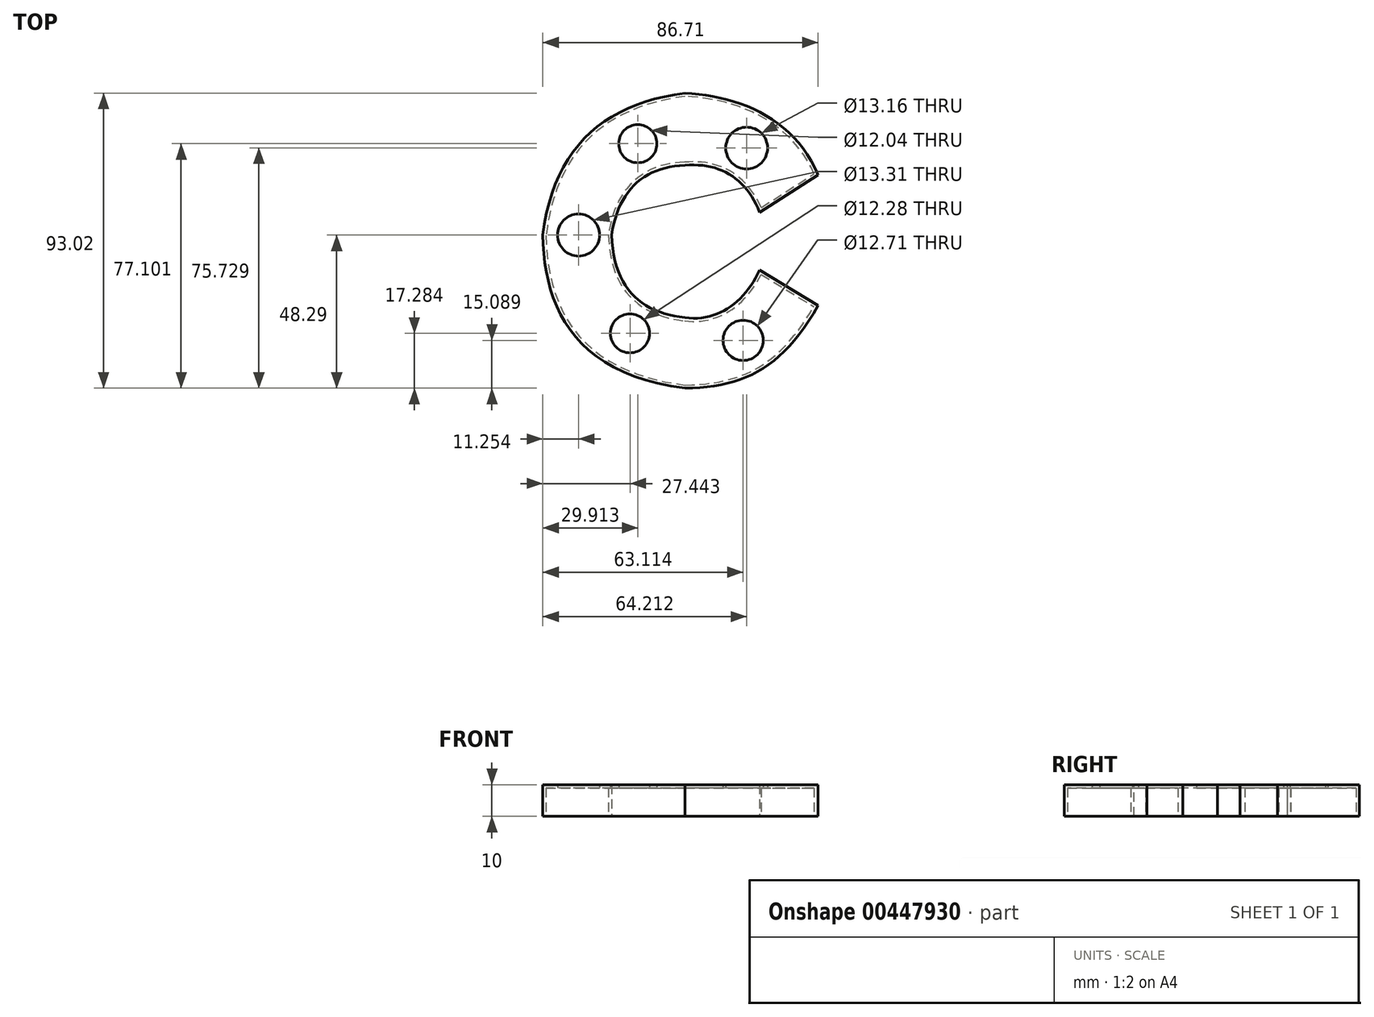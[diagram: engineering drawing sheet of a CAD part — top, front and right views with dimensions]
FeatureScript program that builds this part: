
annotation { "Feature Type Name" : "Feature", "Feature Type Description" : "" }
export const myFeature = defineFeature(function(context is Context, id is Id, definition is map)
    precondition{}
    {
        {
            var Q0;
            Q0=qCreatedBy(makeId("Top.planeOp"),FACE);
            var sketch = newSketch(context, id + "F0", { "sketchPlane" : qUnion([Q0])});
            skLineSegment(sketch, "E0", {"start": v(23.6, 7.13) * mm, "end": v(41.98, 18.93) * mm});
            skLineSegment(sketch, "E1", {"start": v(23.6, -10.98) * mm, "end": v(41.98, -22.23) * mm});
            skFitSpline(sketch, "E2", {"points": [v(41.98, 18.93) * mm, v(0, 44.73) * mm], "startDerivative": vector(-22.23, 53.5) * mm, "endDerivative": vector(-51.04, 2.47) * mm});
            skFitSpline(sketch, "E3", {"points": [v(0, 44.73) * mm, v(-44.73, 0) * mm], "startDerivative": vector(-76.55, -9.88) * mm, "endDerivative": vector(-9.88, -82.32) * mm});
            skFitSpline(sketch, "E4", {"points": [v(-44.73, 0) * mm, v(0, -48.3) * mm], "startDerivative": vector(0.82, -67.5) * mm, "endDerivative": vector(104.54, -13.17) * mm});
            skFitSpline(sketch, "E5", {"points": [v(0, -48.3) * mm, v(41.98, -22.23) * mm], "startDerivative": vector(55.98, 0.82) * mm, "endDerivative": vector(33.75, 59.27) * mm});
            skFitSpline(sketch, "E6", {"points": [v(23.6, 7.13) * mm, v(0, 21.95) * mm], "startDerivative": vector(-12.35, 31.28) * mm, "endDerivative": vector(-33.75, -3.3) * mm});
            skFitSpline(sketch, "E7", {"points": [v(0, 21.95) * mm, v(-23.05, 0) * mm], "startDerivative": vector(-37.87, -0.82) * mm, "endDerivative": vector(-5.76, -41.98) * mm});
            skFitSpline(sketch, "E8", {"points": [v(-23.05, 0) * mm, v(0, -26.07) * mm], "startDerivative": vector(1.65, -51.86) * mm, "endDerivative": vector(40.34, -4.94) * mm});
            skFitSpline(sketch, "E9", {"points": [v(0, -26.07) * mm, v(23.6, -10.98) * mm], "startDerivative": vector(31.28, -4.12) * mm, "endDerivative": vector(14, 30.46) * mm});
            skSolve(sketch);
        }
        {
            var Q0;
            Q0 = qSketchRegion(id + "F0", true);
            var Q1;
            Q1 = qSketchRegion(id + "F3", true);
            extrude(context, id + "F1", {"entities" : qUnion([Q0, Q1]), "depth" : 10 * mm});
        }
        {
            var Q0;
            Q0=makeQuery(id+"F1.opExtrude","CAP_FACE",FACE,{"disambiguationData":[OSD([sQuery(id+"F0.wireOp",EDGE,"E0"),sQuery(id+"F0.wireOp",EDGE,"E1"),sQuery(id+"F0.wireOp",EDGE,"E2"),sQuery(id+"F0.wireOp",EDGE,"E3"),sQuery(id+"F0.wireOp",EDGE,"E4"),sQuery(id+"F0.wireOp",EDGE,"E5"),sQuery(id+"F0.wireOp",EDGE,"E6"),sQuery(id+"F0.wireOp",EDGE,"E7"),sQuery(id+"F0.wireOp",EDGE,"E8"),sQuery(id+"F0.wireOp",EDGE,"E9")])],"isStart":true});
            shell(context, id + "F2", {"entities" : qUnion([Q0]), "thickness" : 1 * mm});
        }
        {
            var Q0;
            Q0=qCreatedBy(makeId("Top.planeOp"),FACE);
            var sketch = newSketch(context, id + "F3", { "sketchPlane" : qUnion([Q0])});
            skCircle(sketch, "E10", {"center": v(19.48, 27.44) * mm, "radius": 6.58 * mm});
            skCircle(sketch, "E11", {"center": v(-14.82, 28.81) * mm, "radius": 6.02 * mm});
            skCircle(sketch, "E12", {"center": v(-33.48, 0) * mm, "radius": 6.65 * mm});
            skCircle(sketch, "E13", {"center": v(-17.29, -31) * mm, "radius": 6.14 * mm});
            skCircle(sketch, "E14", {"center": v(18.38, -33.2) * mm, "radius": 6.35 * mm});
            skSolve(sketch);
        }
        {
            var Q0;
            Q0 = qSketchRegion(id + "F3", true);
            extrude(context, id + "F4", {"entities" : qUnion([Q0]), "operationType" : NewBodyOperationType.REMOVE, "depth" : 25 * mm});
        }
    });
